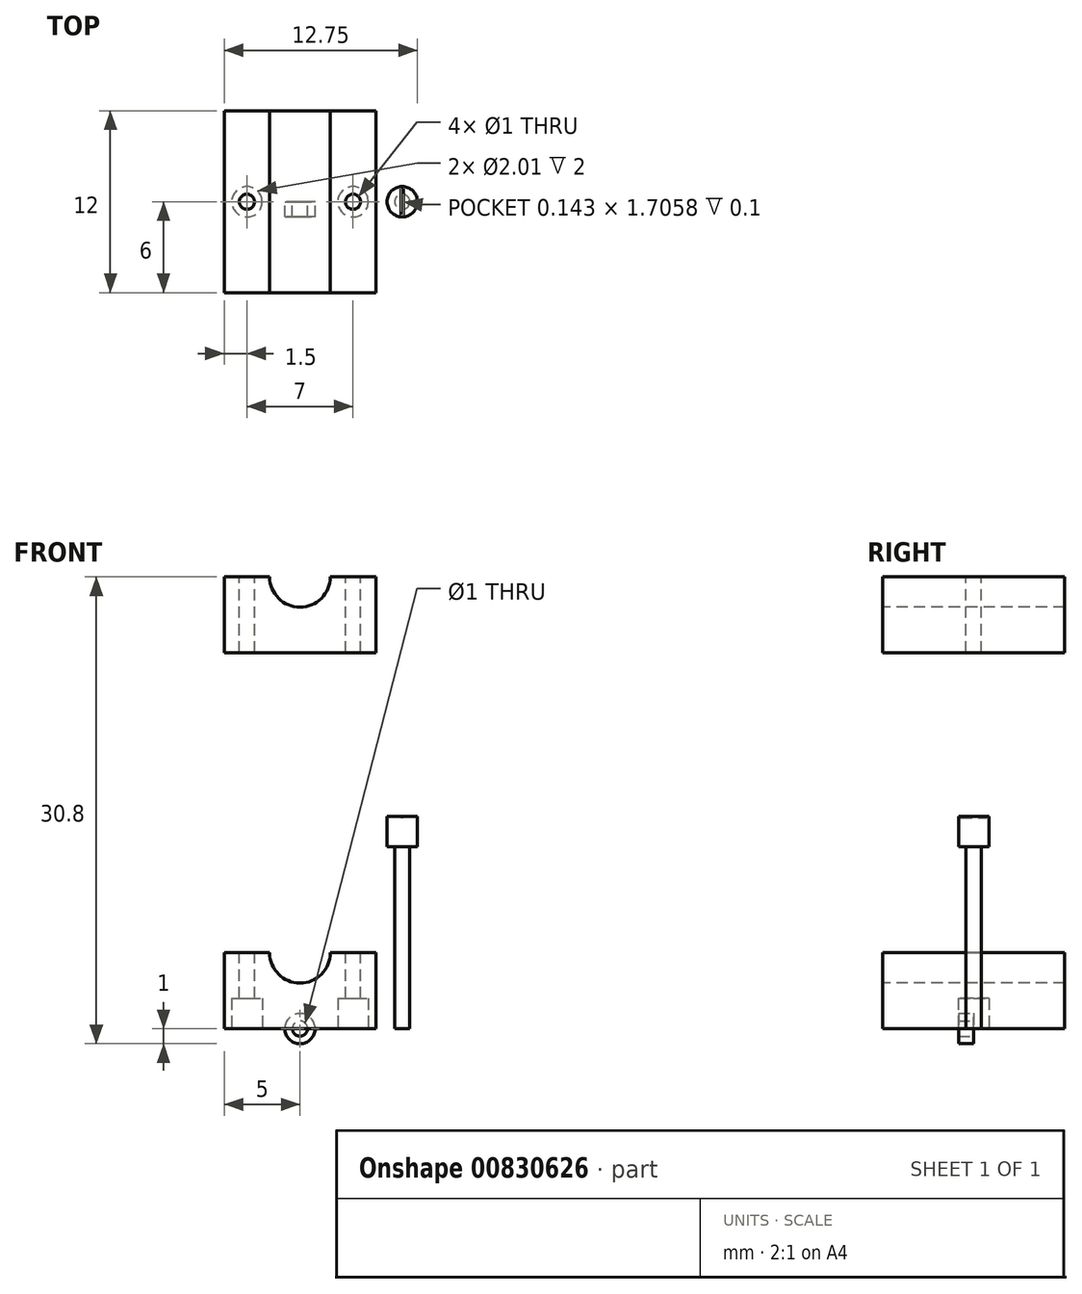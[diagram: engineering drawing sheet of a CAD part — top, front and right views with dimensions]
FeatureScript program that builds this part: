
annotation { "Feature Type Name" : "Feature", "Feature Type Description" : "" }
export const myFeature = defineFeature(function(context is Context, id is Id, definition is map)
    precondition{}
    {
        {
            var Q0;
            Q0=qCreatedBy(makeId("Top.planeOp"),FACE);
            var sketch = newSketch(context, id + "F0", { "sketchPlane" : qUnion([Q0])});
            skLineSegment(sketch, "E0.bottom", {"start": v(5, -6) * mm, "end": v(-5, -6) * mm});
            skLineSegment(sketch, "E0.top", {"start": v(5, 6) * mm, "end": v(-5, 6) * mm});
            skLineSegment(sketch, "E0.left", {"start": v(5, -6) * mm, "end": v(5, 6) * mm});
            skLineSegment(sketch, "E0.right", {"start": v(-5, -6) * mm, "end": v(-5, 6) * mm});
            skPoint(sketch, "E0.middle", {"position": v(0, 0) * mm});
            skSolve(sketch);
        }
        {
            var Q0;
            Q0 = qSketchRegion(id + "F0", true);
            extrude(context, id + "F1", {"entities" : qUnion([Q0]), "depth" : 5 * mm, "offsetDistance" : 25 * mm});
        }
        {
            var Q0;
            Q0=makeQuery(id+"F1.opExtrude","SWEPT_FACE",FACE,{"disambiguationData":[OSD([sQuery(id+"F0.wireOp",EDGE,"E0.bottom")])]});
            var sketch = newSketch(context, id + "F2", { "sketchPlane" : qUnion([Q0])});
            skArc(sketch, "E1", {"start": v(-2, 5) * mm, "mid": v(0, 3) * mm, "end": v(2, 5) * mm});
            skLineSegment(sketch, "E2", {"start": v(-2, 5) * mm, "end": v(2, 5) * mm});
            skSolve(sketch);
        }
        {
            var Q0;
            Q0 = qSketchRegion(id + "F2", true);
            extrude(context, id + "F3", {"entities" : qUnion([Q0]), "operationType" : NewBodyOperationType.REMOVE, "endBound" : BoundingType.THROUGH_ALL, "oppositeDirection" : true, "depth" : 25 * mm, "offsetDistance" : 25 * mm});
        }
        {
            var Q0;
            {var subQ0=sQuery(id+"F0.wireOp",EDGE,"E0.bottom");var subQ1=sQuery(id+"F0.wireOp",EDGE,"E0.right");var subQ2=sQuery(id+"F0.wireOp",EDGE,"E0.top");Q0=makeQuery(id+"F3.boolean.opBoolean","SPLIT",FACE,{"disambiguationData":[TD([makeQuery(id+"F1.opExtrude","SWEPT_FACE",FACE,{"disambiguationData":[OSD([subQ1])]})])],"derivedFrom":makeQuery(id+"F1.opExtrude","CAP_FACE",FACE,{"disambiguationData":[OSD([subQ0,subQ2,sQuery(id+"F0.wireOp",EDGE,"E0.left"),subQ1])],"isStart":false})});}
            var sketch = newSketch(context, id + "F4", { "sketchPlane" : qUnion([Q0])});
            skCircle(sketch, "E3", {"center": v(-3.5, 0) * mm, "radius": 0.5 * mm});
            skSolve(sketch);
        }
        {
            var Q0;
            {var subQ0=sQuery(id+"F0.wireOp",EDGE,"E0.bottom");var subQ1=sQuery(id+"F0.wireOp",EDGE,"E0.top");var subQ2=sQuery(id+"F0.wireOp",EDGE,"E0.left");Q0=makeQuery(id+"F3.boolean.opBoolean","SPLIT",FACE,{"disambiguationData":[TD([makeQuery(id+"F1.opExtrude","SWEPT_FACE",FACE,{"disambiguationData":[OSD([subQ2])]})])],"derivedFrom":makeQuery(id+"F1.opExtrude","CAP_FACE",FACE,{"disambiguationData":[OSD([subQ0,subQ1,subQ2,sQuery(id+"F0.wireOp",EDGE,"E0.right")])],"isStart":false})});}
            var sketch = newSketch(context, id + "F5", { "sketchPlane" : qUnion([Q0])});
            skCircle(sketch, "E4", {"center": v(3.5, 0) * mm, "radius": 0.5 * mm});
            skSolve(sketch);
        }
        {
            var Q0;
            Q0 = qSketchRegion(id + "F4", true);
            extrude(context, id + "F6", {"entities" : qUnion([Q0]), "operationType" : NewBodyOperationType.REMOVE, "endBound" : BoundingType.THROUGH_ALL, "oppositeDirection" : true, "depth" : 25 * mm, "offsetDistance" : 25 * mm});
        }
        {
            var Q0;
            Q0=makeQuery(id+"F5.imprint","IMPRINT",FACE,{"disambiguationData":[TD([[makeQuery(id+"F5.imprint","IMPRINT",EDGE,{"derivedFrom":sQuery(id+"F5.wireOp",EDGE,"E4")}),1.0]])]});
            extrude(context, id + "F7", {"entities" : qUnion([Q0]), "operationType" : NewBodyOperationType.REMOVE, "endBound" : BoundingType.THROUGH_ALL, "oppositeDirection" : true, "depth" : 25 * mm, "offsetDistance" : 25 * mm});
        }
        {
            var Q0;
            Q0=qCreatedBy(makeId("Top.planeOp"),FACE);
            var sketch = newSketch(context, id + "F8", { "sketchPlane" : qUnion([Q0])});
            skCircle(sketch, "E5", {"center": v(6.75, 0) * mm, "radius": 0.5 * mm});
            skSolve(sketch);
        }
        {
            var Q0;
            Q0 = qSketchRegion(id + "F8", true);
            extrude(context, id + "F9", {"entities" : qUnion([Q0]), "depth" : 12 * mm, "offsetDistance" : 25 * mm});
        }
        {
            var Q0;
            Q0=makeQuery(id+"F9.opExtrude","CAP_FACE",FACE,{"disambiguationData":[OSD([sQuery(id+"F8.wireOp",EDGE,"E5")])],"isStart":false});
            var sketch = newSketch(context, id + "F10", { "sketchPlane" : qUnion([Q0])});
            skCircle(sketch, "E6", {"center": v(6.75, 0) * mm, "radius": 1 * mm});
            skSolve(sketch);
        }
        {
            var Q0;
            Q0 = qSketchRegion(id + "F10", true);
            extrude(context, id + "F11", {"entities" : qUnion([Q0]), "operationType" : NewBodyOperationType.ADD, "depth" : 2 * mm, "offsetDistance" : 25 * mm});
        }
        {
            var Q0;
            Q0=qCreatedBy(makeId("Front.planeOp"),FACE);
            var sketch = newSketch(context, id + "F12", { "sketchPlane" : qUnion([Q0])});
            skCircle(sketch, "E7", {"center": v(0, 0) * mm, "radius": 0.5 * mm});
            skCircle(sketch, "E8", {"center": v(0, 0) * mm, "radius": 1 * mm});
            skSolve(sketch);
        }
        {
            var Q0;
            Q0 = qSketchRegion(id + "F12", true);
            extrude(context, id + "F13", {"entities" : qUnion([Q0]), "depth" : 1 * mm, "offsetDistance" : 25 * mm});
        }
        {
            var Q0;
            Q0=makeQuery(id+"F1.opExtrude","SWEPT_BODY",BODY,{"disambiguationData":[OSD([sQuery(id+"F0.wireOp",EDGE,"E0.bottom"),sQuery(id+"F0.wireOp",EDGE,"E0.top"),sQuery(id+"F0.wireOp",EDGE,"E0.left"),sQuery(id+"F0.wireOp",EDGE,"E0.right")])]});
            transform(context, id + "F14", {"entities" : qUnion([Q0]), "transformType" : TransformType.TRANSLATION_3D, "dx" : 0 * mm, "dy" : 0 * mm, "dz" : 24.8 * mm, "makeCopy" : true});
        }
        {
            var Q0;
            Q0=makeQuery(id+"F1.opExtrude","CAP_FACE",FACE,{"disambiguationData":[OSD([sQuery(id+"F0.wireOp",EDGE,"E0.bottom"),sQuery(id+"F0.wireOp",EDGE,"E0.top"),sQuery(id+"F0.wireOp",EDGE,"E0.left"),sQuery(id+"F0.wireOp",EDGE,"E0.right")])],"isStart":true});
            var sketch = newSketch(context, id + "F15", { "sketchPlane" : qUnion([Q0])});
            skCircle(sketch, "E9", {"center": v(-3.5, 0) * mm, "radius": 1 * mm});
            skCircle(sketch, "E10", {"center": v(3.5, 0) * mm, "radius": 1 * mm});
            skSolve(sketch);
        }
        {
            var Q0;
            Q0 = qSketchRegion(id + "F15", true);
            extrude(context, id + "F16", {"entities" : qUnion([Q0]), "operationType" : NewBodyOperationType.REMOVE, "oppositeDirection" : true, "depth" : 2 * mm, "offsetDistance" : 25 * mm});
        }
        {
            var Q0;
            Q0=makeQuery(id+"F11.opExtrude","CAP_FACE",FACE,{"disambiguationData":[OSD([sQuery(id+"F10.wireOp",EDGE,"E6")])],"isStart":false});
            var sketch = newSketch(context, id + "F17", { "sketchPlane" : qUnion([Q0])});
            skLineSegment(sketch, "E11.bottom", {"start": v(6.82, -0.85) * mm, "end": v(6.67, -0.85) * mm});
            skLineSegment(sketch, "E11.top", {"start": v(6.82, 0.85) * mm, "end": v(6.67, 0.85) * mm});
            skLineSegment(sketch, "E11.left", {"start": v(6.82, -0.85) * mm, "end": v(6.82, 0.85) * mm});
            skLineSegment(sketch, "E11.right", {"start": v(6.67, -0.85) * mm, "end": v(6.67, 0.85) * mm});
            skPoint(sketch, "E11.middle", {"position": v(6.75, 0) * mm});
            skSolve(sketch);
        }
        {
            var Q0;
            Q0 = qSketchRegion(id + "F17", true);
            extrude(context, id + "F18", {"entities" : qUnion([Q0]), "operationType" : NewBodyOperationType.REMOVE, "oppositeDirection" : true, "depth" : 0.1 * mm, "offsetDistance" : 25 * mm});
        }
    });
